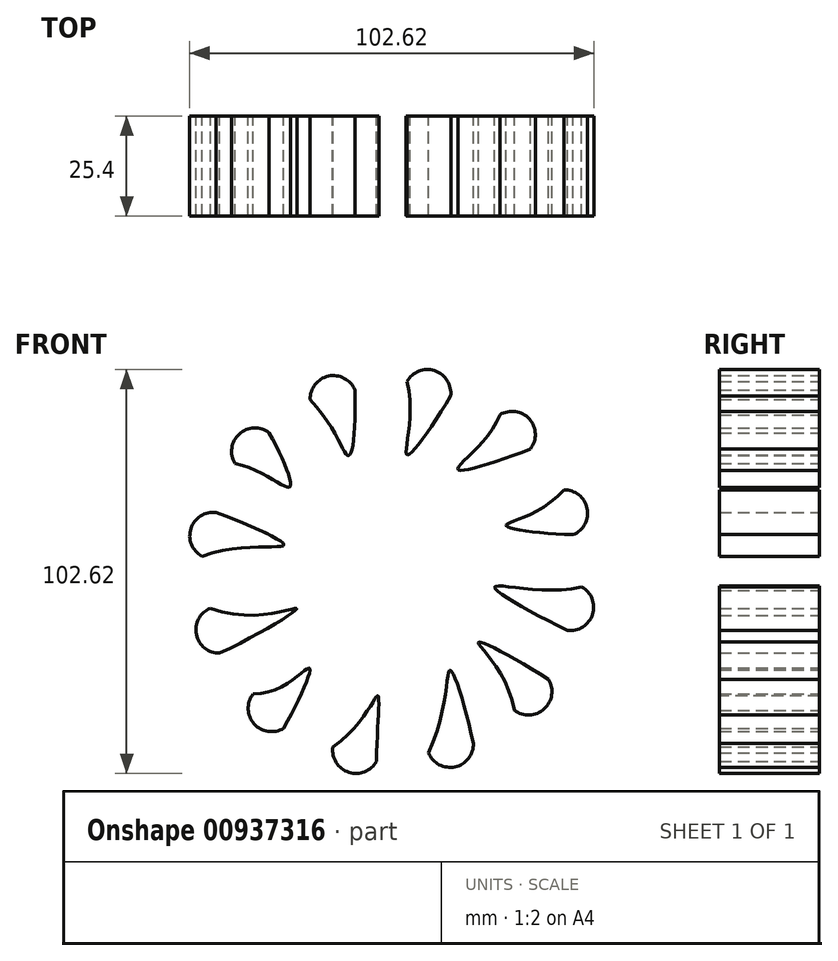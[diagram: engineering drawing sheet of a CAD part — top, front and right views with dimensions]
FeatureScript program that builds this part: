
annotation { "Feature Type Name" : "Feature", "Feature Type Description" : "" }
export const myFeature = defineFeature(function(context is Context, id is Id, definition is map)
    precondition{}
    {
        {
            var Q0;
            Q0=qCreatedBy(makeId("Front.planeOp"),FACE);
            var sketch = newSketch(context, id + "F0", { "sketchPlane" : qUnion([Q0])});
            skArc(sketch, "E0.2.0", {"start": v(46.1, 9.36) * mm, "mid": v(49.64, 16.05) * mm, "end": v(43.7, 20.75) * mm});
            skPoint(sketch, "E0.center", {"position": v(0, 0) * mm});
            skFitSpline(sketch, "E1", {"points": [v(43.7, 20.75) * mm, v(29.04, 11.7) * mm, v(46.1, 9.36) * mm], "startDerivative": vector(-36.24, -41.82) * mm, "endDerivative": vector(49.99, -1.35) * mm});
            skArc(sketch, "E2.1.0", {"start": v(-31.15, 35.24) * mm, "mid": v(-38.72, 34.96) * mm, "end": v(-39.82, 27.46) * mm});
            skArc(sketch, "E2.1.1", {"start": v(-31.15, 35.24) * mm, "mid": v(-38.72, 34.96) * mm, "end": v(-39.82, 27.46) * mm});
            skArc(sketch, "E2.1.2", {"start": v(-31.15, 35.24) * mm, "mid": v(-38.72, 34.96) * mm, "end": v(-39.82, 27.46) * mm});
            skArc(sketch, "E2.2.0", {"start": v(-14.95, -44.6) * mm, "mid": v(-10.92, -51.02) * mm, "end": v(-3.88, -48.22) * mm});
            skArc(sketch, "E2.2.1", {"start": v(-14.95, -44.6) * mm, "mid": v(-10.92, -51.02) * mm, "end": v(-3.88, -48.22) * mm});
            skArc(sketch, "E2.2.2", {"start": v(-14.95, -44.6) * mm, "mid": v(-10.92, -51.02) * mm, "end": v(-3.88, -48.22) * mm});
            skFitSpline(sketch, "E3", {"points": [v(-31.15, 35.24) * mm, v(-25.9, 21.48) * mm, v(-39.82, 27.46) * mm], "startDerivative": vector(20.06, -37.56) * mm, "endDerivative": vector(-43.64, 9.4) * mm});
            skFitSpline(sketch, "E4", {"points": [v(-14.95, -44.6) * mm, v(-3.54, -31.58) * mm, v(-3.88, -48.22) * mm], "startDerivative": vector(49.19, 35.51) * mm, "endDerivative": vector(-0.46, -51.81) * mm});
            skArc(sketch, "E5.1.0", {"start": v(-9.36, 46.1) * mm, "mid": v(-16.05, 49.64) * mm, "end": v(-20.75, 43.7) * mm});
            skArc(sketch, "E5.1.1", {"start": v(44.6, -14.95) * mm, "mid": v(51.02, -10.92) * mm, "end": v(48.22, -3.88) * mm});
            skArc(sketch, "E5.1.2", {"start": v(-35.24, -31.15) * mm, "mid": v(-34.96, -38.72) * mm, "end": v(-27.46, -39.82) * mm});
            skArc(sketch, "E5.1.4", {"start": v(44.6, -14.95) * mm, "mid": v(51.02, -10.92) * mm, "end": v(48.22, -3.88) * mm});
            skArc(sketch, "E5.1.5", {"start": v(-35.24, -31.15) * mm, "mid": v(-34.96, -38.72) * mm, "end": v(-27.46, -39.82) * mm});
            skArc(sketch, "E5.1.6", {"start": v(-9.36, 46.1) * mm, "mid": v(-16.05, 49.64) * mm, "end": v(-20.75, 43.7) * mm});
            skArc(sketch, "E5.1.9", {"start": v(44.6, -14.95) * mm, "mid": v(51.02, -10.92) * mm, "end": v(48.22, -3.88) * mm});
            skArc(sketch, "E5.1.10", {"start": v(-9.36, 46.1) * mm, "mid": v(-16.05, 49.64) * mm, "end": v(-20.75, 43.7) * mm});
            skArc(sketch, "E5.1.11", {"start": v(-35.24, -31.15) * mm, "mid": v(-34.96, -38.72) * mm, "end": v(-27.46, -39.82) * mm});
            skArc(sketch, "E5.1.13", {"start": v(-35.24, -31.15) * mm, "mid": v(-34.96, -38.72) * mm, "end": v(-27.46, -39.82) * mm});
            skArc(sketch, "E5.1.14", {"start": v(-35.24, -31.15) * mm, "mid": v(-34.96, -38.72) * mm, "end": v(-27.46, -39.82) * mm});
            skArc(sketch, "E5.2.0", {"start": v(-46.1, -9.36) * mm, "mid": v(-49.64, -16.05) * mm, "end": v(-43.7, -20.75) * mm});
            skArc(sketch, "E5.2.1", {"start": v(14.95, 44.6) * mm, "mid": v(10.92, 51.02) * mm, "end": v(3.88, 48.22) * mm});
            skArc(sketch, "E5.2.2", {"start": v(31.15, -35.24) * mm, "mid": v(38.72, -34.96) * mm, "end": v(39.82, -27.46) * mm});
            skArc(sketch, "E5.2.4", {"start": v(14.95, 44.6) * mm, "mid": v(10.92, 51.02) * mm, "end": v(3.88, 48.22) * mm});
            skArc(sketch, "E5.2.5", {"start": v(31.15, -35.24) * mm, "mid": v(38.72, -34.96) * mm, "end": v(39.82, -27.46) * mm});
            skArc(sketch, "E5.2.6", {"start": v(-46.1, -9.36) * mm, "mid": v(-49.64, -16.05) * mm, "end": v(-43.7, -20.75) * mm});
            skArc(sketch, "E5.2.9", {"start": v(14.95, 44.6) * mm, "mid": v(10.92, 51.02) * mm, "end": v(3.88, 48.22) * mm});
            skArc(sketch, "E5.2.10", {"start": v(-46.1, -9.36) * mm, "mid": v(-49.64, -16.05) * mm, "end": v(-43.7, -20.75) * mm});
            skArc(sketch, "E5.2.11", {"start": v(31.15, -35.24) * mm, "mid": v(38.72, -34.96) * mm, "end": v(39.82, -27.46) * mm});
            skArc(sketch, "E5.2.13", {"start": v(31.15, -35.24) * mm, "mid": v(38.72, -34.96) * mm, "end": v(39.82, -27.46) * mm});
            skArc(sketch, "E5.2.14", {"start": v(31.15, -35.24) * mm, "mid": v(38.72, -34.96) * mm, "end": v(39.82, -27.46) * mm});
            skArc(sketch, "E6.4.3.0", {"start": v(-44.6, 14.95) * mm, "mid": v(-51.02, 10.92) * mm, "end": v(-48.22, 3.88) * mm});
            skArc(sketch, "E6.6.3.0", {"start": v(9.36, -46.1) * mm, "mid": v(16.05, -49.64) * mm, "end": v(20.75, -43.7) * mm});
            skArc(sketch, "E6.8.3.0", {"start": v(35.24, 31.15) * mm, "mid": v(34.96, 38.72) * mm, "end": v(27.46, 39.82) * mm});
            skArc(sketch, "E6.13.3.0", {"start": v(-44.6, 14.95) * mm, "mid": v(-51.02, 10.92) * mm, "end": v(-48.22, 3.88) * mm});
            skArc(sketch, "E6.17.3.0", {"start": v(35.24, 31.15) * mm, "mid": v(34.96, 38.72) * mm, "end": v(27.46, 39.82) * mm});
            skArc(sketch, "E6.21.3.0", {"start": v(9.36, -46.1) * mm, "mid": v(16.05, -49.64) * mm, "end": v(20.75, -43.7) * mm});
            skArc(sketch, "E6.27.3.0", {"start": v(-44.6, 14.95) * mm, "mid": v(-51.02, 10.92) * mm, "end": v(-48.22, 3.88) * mm});
            skArc(sketch, "E6.31.3.0", {"start": v(9.36, -46.1) * mm, "mid": v(16.05, -49.64) * mm, "end": v(20.75, -43.7) * mm});
            skArc(sketch, "E6.35.3.0", {"start": v(35.24, 31.15) * mm, "mid": v(34.96, 38.72) * mm, "end": v(27.46, 39.82) * mm});
            skArc(sketch, "E6.40.3.0", {"start": v(35.24, 31.15) * mm, "mid": v(34.96, 38.72) * mm, "end": v(27.46, 39.82) * mm});
            skArc(sketch, "E6.44.3.0", {"start": v(35.24, 31.15) * mm, "mid": v(34.96, 38.72) * mm, "end": v(27.46, 39.82) * mm});
            skFitSpline(sketch, "E7", {"points": [v(-20.75, 43.7) * mm, v(-11.1, 29.42) * mm, v(-9.36, 46.1) * mm], "startDerivative": vector(40.64, -43.33) * mm, "endDerivative": vector(-2.01, 62.93) * mm});
            skFitSpline(sketch, "E8", {"points": [v(3.88, 48.22) * mm, v(3.88, 29.68) * mm, v(14.95, 44.6) * mm], "startDerivative": vector(13.4, -53.34) * mm, "endDerivative": vector(27.67, 46.55) * mm});
            skFitSpline(sketch, "E9", {"points": [v(27.46, 39.82) * mm, v(16.8, 26.03) * mm, v(35.24, 31.15) * mm], "startDerivative": vector(-15.89, -43.04) * mm, "endDerivative": vector(50.87, 19.78) * mm});
            skFitSpline(sketch, "E10", {"points": [v(48.22, -3.88) * mm, v(26.18, -3.88) * mm, v(44.6, -14.95) * mm], "startDerivative": vector(-56.76, -14.42) * mm, "endDerivative": vector(57.16, -27.82) * mm});
            skFitSpline(sketch, "E11", {"points": [v(39.82, -27.46) * mm, v(22.01, -18.03) * mm, v(31.15, -35.24) * mm], "startDerivative": vector(-48.87, 32.2) * mm, "endDerivative": vector(11.14, -63.16) * mm});
            skFitSpline(sketch, "E12", {"points": [v(20.75, -43.7) * mm, v(14.83, -25.07) * mm, v(9.36, -46.1) * mm], "startDerivative": vector(-12.52, 57.56) * mm, "endDerivative": vector(-29.77, -65.03) * mm});
            skFitSpline(sketch, "E13", {"points": [v(-27.46, -39.82) * mm, v(-21, -24.54) * mm, v(-35.24, -31.15) * mm], "startDerivative": vector(23.28, 41.17) * mm, "endDerivative": vector(-46.96, 1.04) * mm});
            skFitSpline(sketch, "E14", {"points": [v(-43.7, -20.75) * mm, v(-24.14, -9.42) * mm, v(-46.1, -9.36) * mm], "startDerivative": vector(59.76, 28.13) * mm, "endDerivative": vector(-68.13, 25.62) * mm});
            skFitSpline(sketch, "E15", {"points": [v(-48.22, 3.88) * mm, v(-27.46, 6.74) * mm, v(-44.6, 14.95) * mm], "startDerivative": vector(60.1, 21.37) * mm, "endDerivative": vector(-53.58, 19.56) * mm});
            skSolve(sketch);
        }
        {
            var Q0;
            Q0 = qSketchRegion(id + "F0", true);
            extrude(context, id + "F1", {"entities" : qUnion([Q0]), "depth" : 25.4 * mm, "offsetDistance" : 25.4 * mm});
        }
    });
